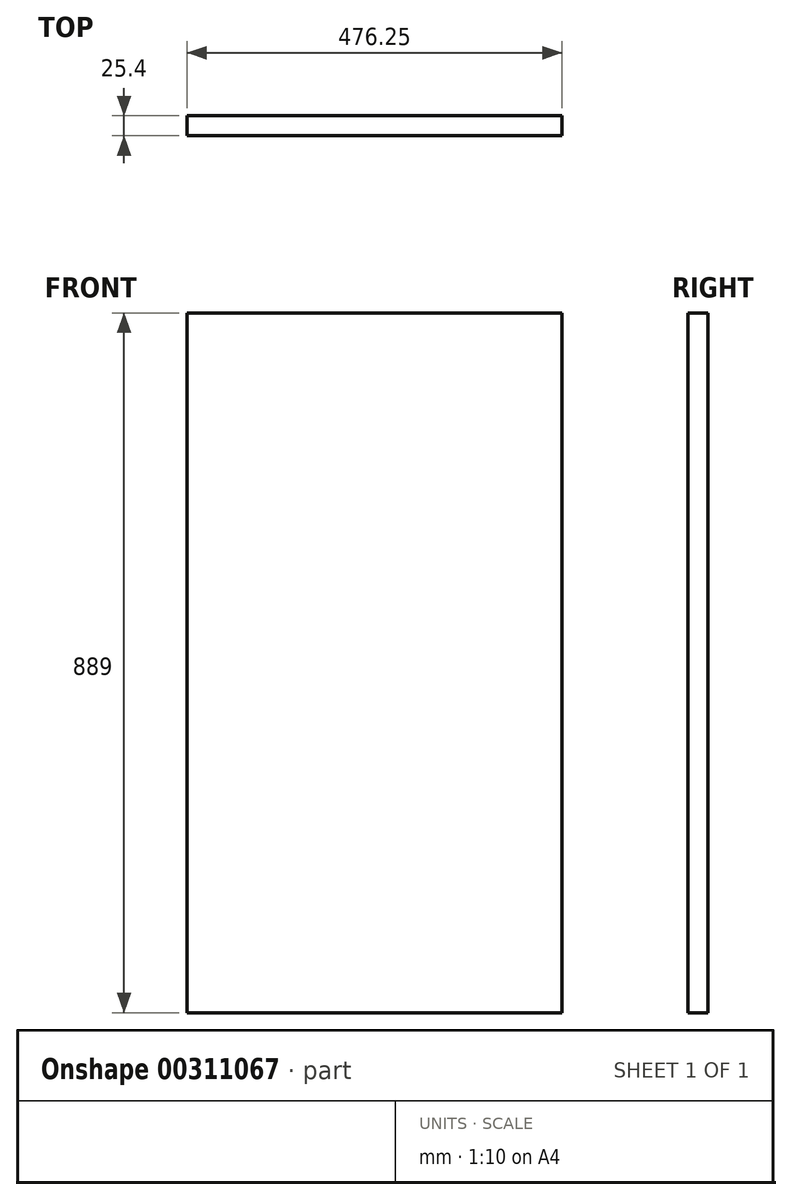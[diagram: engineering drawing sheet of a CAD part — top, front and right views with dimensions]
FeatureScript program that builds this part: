
annotation { "Feature Type Name" : "Feature", "Feature Type Description" : "" }
export const myFeature = defineFeature(function(context is Context, id is Id, definition is map)
    precondition{}
    {
        {
            var Q0;
            Q0=qCreatedBy(makeId("Front.planeOp"),FACE);
            var sketch = newSketch(context, id + "F0", { "sketchPlane" : qUnion([Q0])});
            skLineSegment(sketch, "E0.bottom", {"start": v(0, 0) * mm, "end": v(476.25, 0) * mm});
            skLineSegment(sketch, "E0.top", {"start": v(0, 889) * mm, "end": v(476.25, 889) * mm});
            skLineSegment(sketch, "E0.left", {"start": v(0, 0) * mm, "end": v(0, 889) * mm});
            skLineSegment(sketch, "E0.right", {"start": v(476.25, 0) * mm, "end": v(476.25, 889) * mm});
            skSolve(sketch);
        }
        {
            var Q0;
            Q0 = qSketchRegion(id + "F0", true);
            extrude(context, id + "F1", {"entities" : qUnion([Q0]), "depth" : 25.4 * mm});
        }
    });
